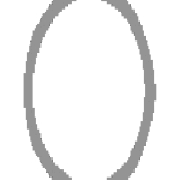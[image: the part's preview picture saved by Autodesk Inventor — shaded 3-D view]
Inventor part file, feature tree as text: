
AUTODESK INVENTOR PART (.ipt)
format: ipt  version: 2021 (Build 250183000, 183)  size: 112,640 bytes
history: native  units: in
note: dims shown in document units (in); Inventor stores cm internally (conversion verified against a paired STEP export)
features: other x4, sketch x3, plane x1
ambient origin geometry x8: Origin, YZ Plane, XZ Plane, XY Plane, X Axis, Y Axis, Z Axis, Center Point
bodies: Solid1 (feature_tree), Body (feature_tree)
feature tree (8):
  other  "Driven Length"
  other  "Frame Generator"
  other  "Start Plane"
  other  "End Plane"
  sketch  "Sketch"  dims[d2=18.6078in d4=-0.0in d5=18.6078in d6=0.12in d7=0.0in d8=90.0deg d9=18.6078in]
  sketch  "Sketch2"  dims[d0=1.0in]
  plane  "Work Plane3"
  sketch  "Sketch3"  dims[d1=0.065in]
